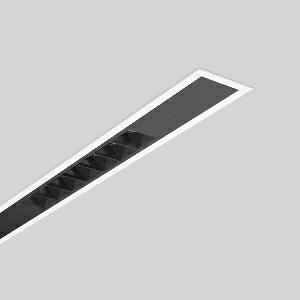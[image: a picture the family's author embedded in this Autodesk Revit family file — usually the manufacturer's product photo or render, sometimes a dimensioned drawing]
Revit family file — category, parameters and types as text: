
# Revit family: less_is_more_beamline_312470_002_6bd0
name_source: partatom
category: Lighting Fixtures
units: mm (PartAtom-declared; Revit-internal decimal feet)

## family parameters
Cut with Voids When Loaded = No
Host = Face
Light Source = No
Part Type = Normal
Room Calculation Point = No
Round Connector Dimension = Use Diameter
Shared = No

## types (1)
- LESS IS MORE BEAMLINE (1 x LED Modul 930, 1825 lm, 3000)
    Apparent Load = 48 VA
    CIE Flux Codes = 100 100 100 100 100
    Color Rendering = 90
    Color Temperature = 3000
    Default Elevation = 1800 mm
    Description = Series: LESS IS MORE BEAMLINE
Linear recessed ceiling and wall luminaire for aesthetically sophisticated lighting. Luminaire with two LED light units. Housing: extruded aluminium profile, powder-coated. End cap aluminium powder-coated. LED light unit with MRS technology: Mini-Reflector-System made of metallised thermoplastic with prismatic black glare-suppressing frame for pleasant glare-free light (RUG < 10). Each LED light unit has 7 reflector elements. Wide beam light distribution. Ceiling installation with pre-assembled SBS mounting system. LED unit with integrated converter interchangeable and removable. Suitable for through-wiring. 
Colour: traffic white, matt (RAL 9016)
Length: 1141 mm
Width: 71 mm
Height: 1.5 mm
Cut-out length: 1128 mm
Cut-out width: 60 mm
Recess height: 125 mm
Luminaire: recess height: 106 mm
Lamp: LED
Socket: without socket
Colour temperature: 3000K
Colour rendering index (CRI): 90
System power: 48 W
Rated luminous flux: 3650 lm
Luminous efficiency: 76 lm/W
Control gear: Regulated power supply
Protection class: I
Type of protection: IP 20
    Height = 0 mm  [stored 0 ft]
    Lamp = 1 x LED Modul 930
    Lamp Light Flux = 1825 lm
    Lamp count = 1
    Length = 1141 mm
    Lifetime = 50000 h
    Luminous efficacy = 76 lm/W
    Manufacturer = RZB
    ModVariant = No
    Model = 312470.002
    Mounting Place = Ceiling, Wall
    Mounting Type = Recessed
    Number of Poles = 1
    OnlyDefault = Yes
    Power Factor = 1
    Product Name = LESS IS MORE BEAMLINE
    Product group = Recessed LED linear luminaires
    ProductGroupID = 407
    Protection Class = Protection class I
    Protection Degree = IP 20
    RLX_Detail_Level = 1
    RLX_Emergency_Light_Flux = 0 lm
    RLX_Emergency_Type = 0
    RLX_Emergency_Type_DB = No
    RlxData = <blob elided: 23689 chars, md5=3768cd95>
    Socket = socket
    Standby Power = 0 W
    System Light Flux = 3650 lm
    System Power = 48 W
    Type Comments = Product without accessories
    Type Image = 312465.002.jpg
    URL = http://relux.com
    VarID = ---
    Voltage = 230 V
    Voltage Range = 220-240 V
    Weight = 0.00 kg
    Width = 71 mm

note: [stored X ft] marks values corroborated as IEEE doubles in the binary element streams (Revit-internal decimal feet)

## geometry (parser evidence)
native form markers: Blend x4, Sweep x14
no freeform markers — native parametric forms only
